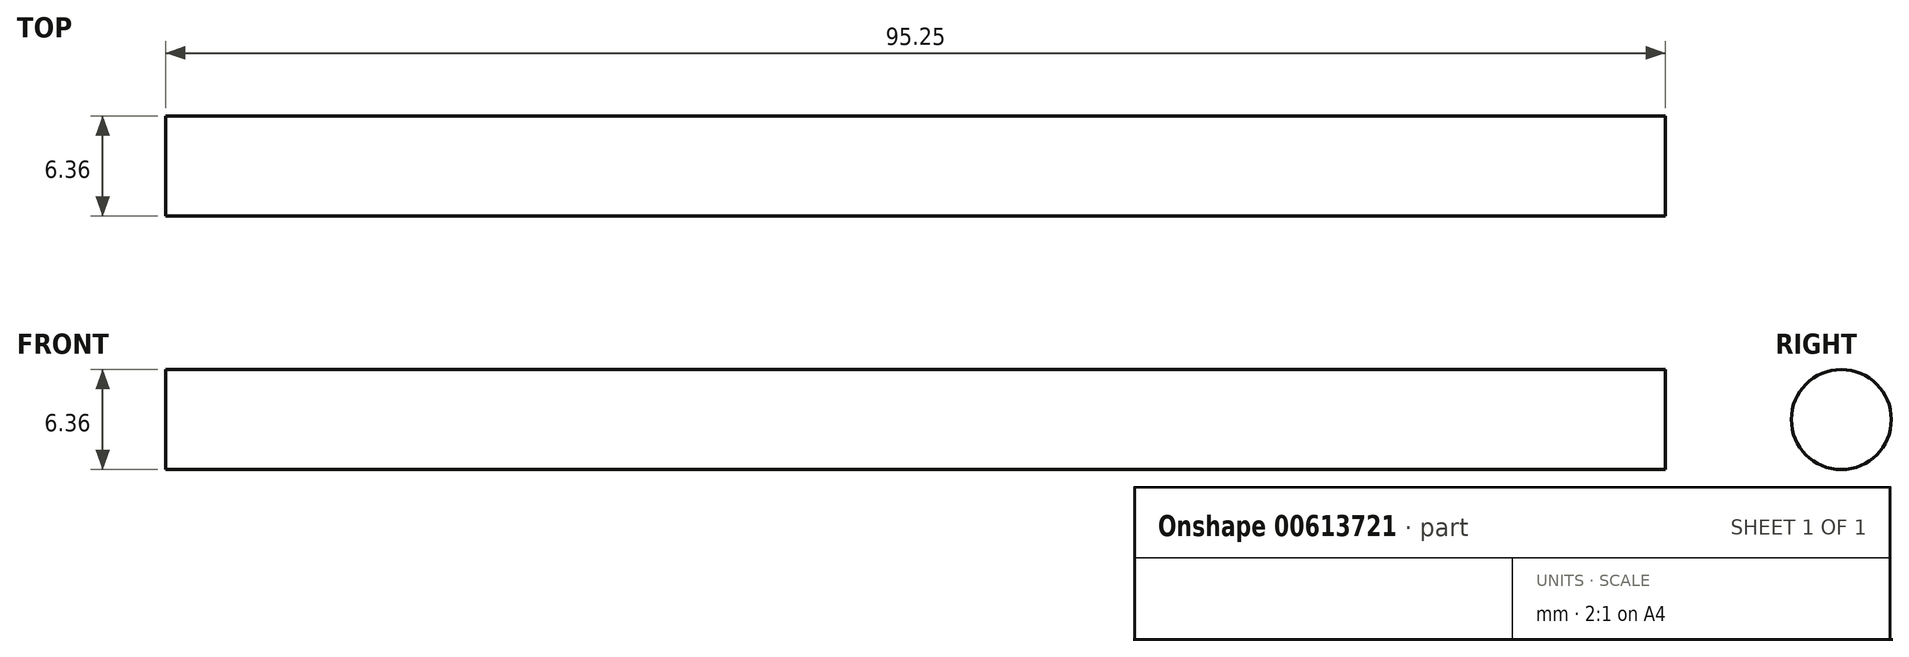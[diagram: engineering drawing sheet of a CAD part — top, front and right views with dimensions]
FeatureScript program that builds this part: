
annotation { "Feature Type Name" : "Feature", "Feature Type Description" : "" }
export const myFeature = defineFeature(function(context is Context, id is Id, definition is map)
    precondition{}
    {
        {
            var Q0;
            Q0=qCreatedBy(makeId("Right.planeOp"),FACE);
            var sketch = newSketch(context, id + "F0", { "sketchPlane" : qUnion([Q0])});
            skCircle(sketch, "E0", {"center": v(0, 0) * mm, "radius": 3.18 * mm});
            skSolve(sketch);
        }
        {
            var Q0;
            Q0 = qSketchRegion(id + "F0", true);
            extrude(context, id + "F1", {"entities" : qUnion([Q0]), "depth" : 95.25 * mm, "offsetDistance" : 25.4 * mm});
        }
    });
